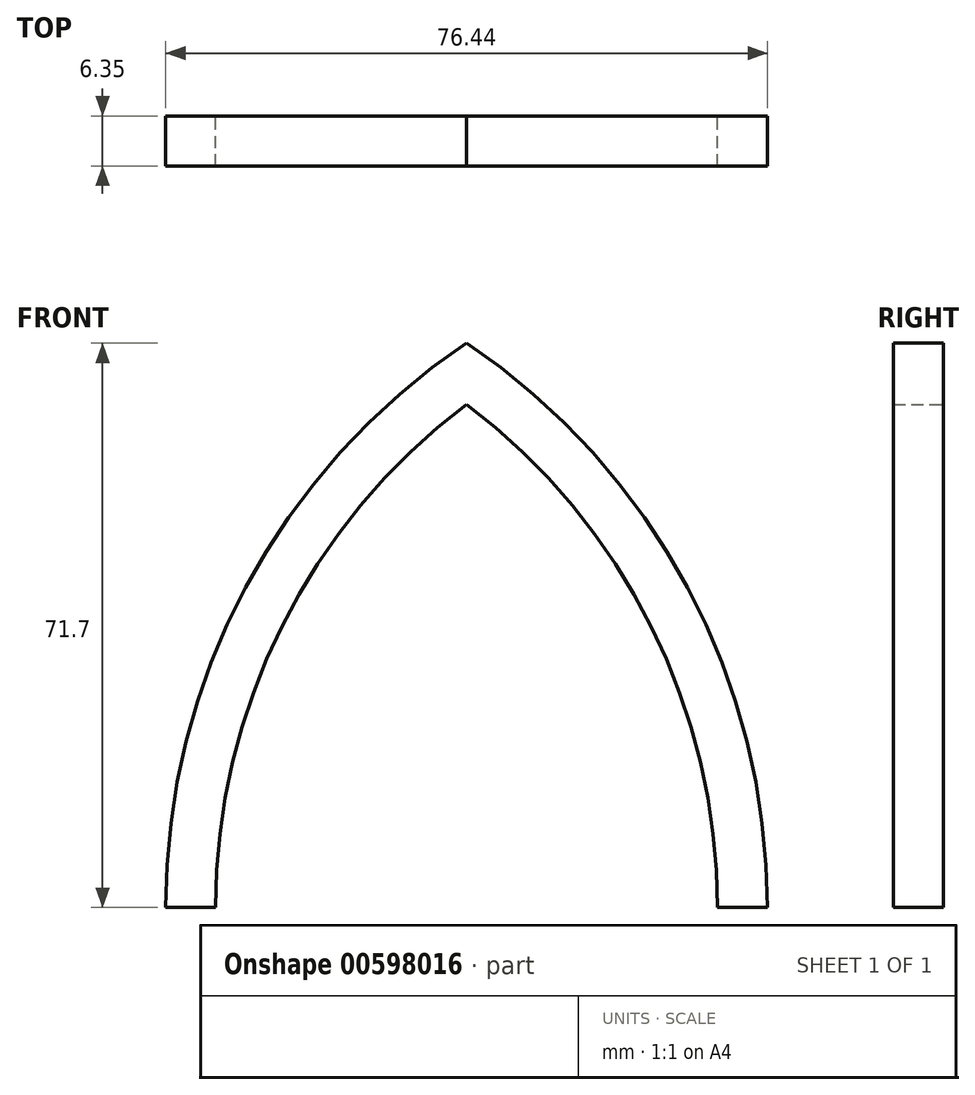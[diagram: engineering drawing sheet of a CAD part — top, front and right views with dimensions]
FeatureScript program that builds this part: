
annotation { "Feature Type Name" : "Feature", "Feature Type Description" : "" }
export const myFeature = defineFeature(function(context is Context, id is Id, definition is map)
    precondition{}
    {
        {
            var Q0;
            Q0=qCreatedBy(makeId("Front.planeOp"),FACE);
            var sketch = newSketch(context, id + "F0", { "sketchPlane" : qUnion([Q0])});
            skArc(sketch, "E0", {"start": v(0, 76.2) * mm, "mid": v(-29.1, 43.13) * mm, "end": v(-38.1, 0) * mm});
            skArc(sketch, "E1", {"start": v(38.1, 0) * mm, "mid": v(29.1, 43.13) * mm, "end": v(0, 76.2) * mm});
            skArc(sketch, "E2.0", {"start": v(0, 68.4) * mm, "mid": v(-23.46, 40.2) * mm, "end": v(-31.87, 4.5) * mm});
            skArc(sketch, "E2.1", {"start": v(31.87, 4.5) * mm, "mid": v(23.46, 40.2) * mm, "end": v(0, 68.4) * mm});
            skLineSegment(sketch, "E2.2", {"start": v(-31.87, 4.5) * mm, "end": v(31.87, 4.5) * mm});
            skLineSegment(sketch, "E3", {"start": v(-31.87, 4.5) * mm, "end": v(-38.22, 4.5) * mm});
            skLineSegment(sketch, "E4", {"start": v(31.87, 4.5) * mm, "end": v(38.22, 4.5) * mm});
            skSolve(sketch);
        }
        {
            var Q0;
            Q0=makeQuery(id+"F0.imprint","IMPRINT",FACE,{"disambiguationData":[TD([[makeQuery(id+"F0.imprint","IMPRINT",EDGE,{"derivedFrom":sQuery(id+"F0.wireOp",EDGE,"E0")}),1.0]])]});
            extrude(context, id + "F1", {"entities" : qUnion([Q0]), "depth" : 6.35 * mm, "offsetDistance" : 25.4 * mm});
        }
    });
